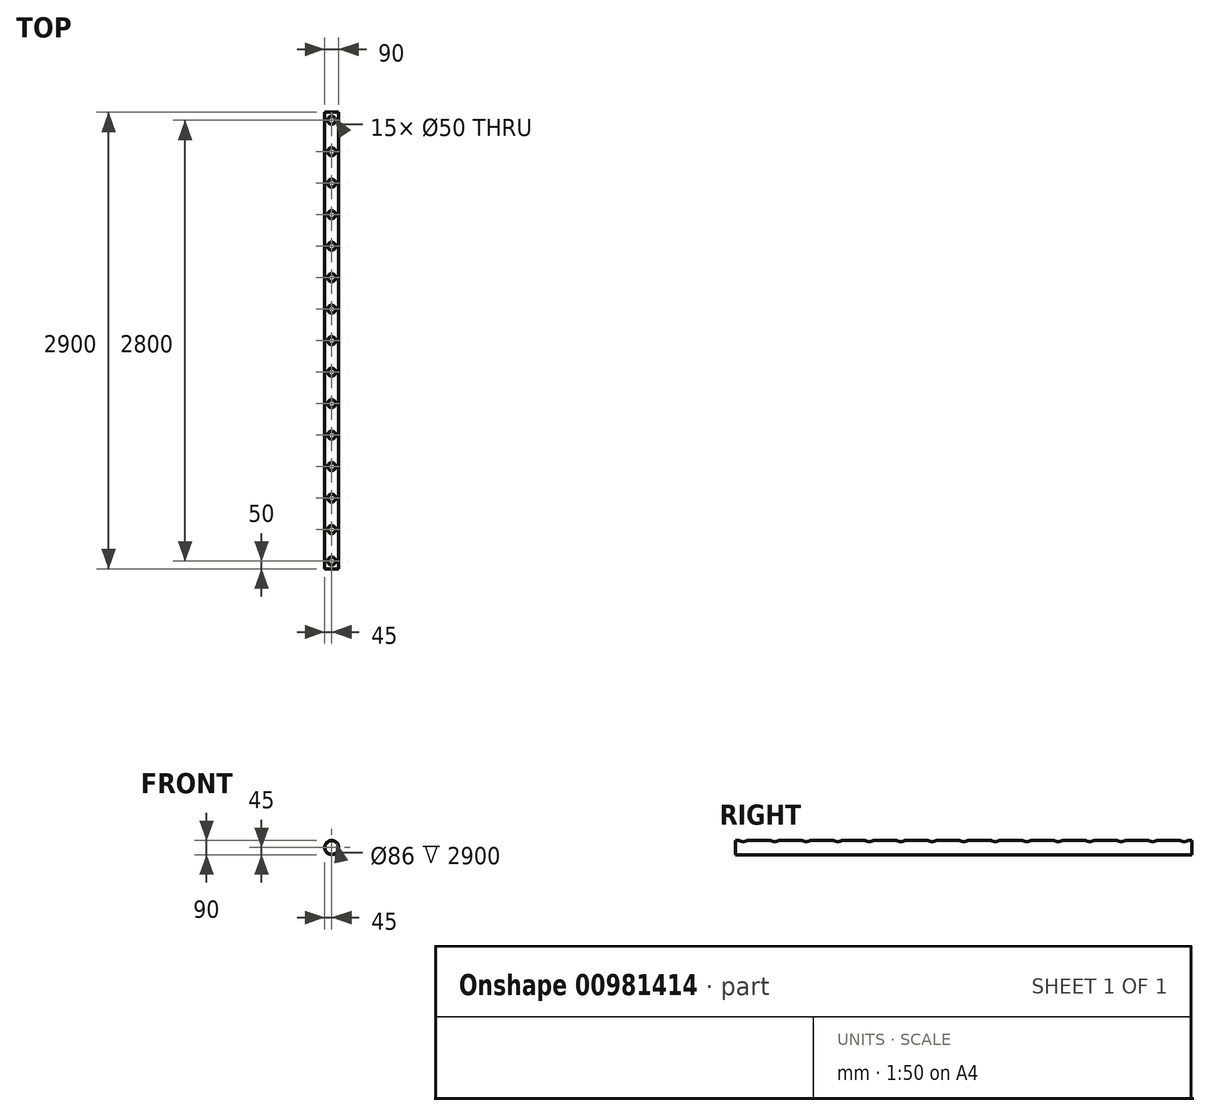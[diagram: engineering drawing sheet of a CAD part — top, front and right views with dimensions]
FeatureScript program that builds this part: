
annotation { "Feature Type Name" : "Feature", "Feature Type Description" : "" }
export const myFeature = defineFeature(function(context is Context, id is Id, definition is map)
    precondition{}
    {
        {
            var Q0;
            Q0=qCreatedBy(makeId("Front.planeOp"),FACE);
            var sketch = newSketch(context, id + "F0", { "sketchPlane" : qUnion([Q0])});
            skCircle(sketch, "E0", {"center": v(0, 0) * mm, "radius": 45 * mm});
            skCircle(sketch, "E1.0", {"center": v(0, 0) * mm, "radius": 43 * mm});
            skSolve(sketch);
        }
        {
            var Q0;
            Q0=qSketchRegion(id+"F0",true);
            extrude(context, id + "F1", {"entities" : qUnion([Q0]), "endBound" : BoundingType.SYMMETRIC, "depth" : 2900 * mm, "offsetDistance" : 25 * mm});
        }
        {
            var Q0;
            Q0=qCreatedBy(makeId("Top.planeOp"),FACE);
            cPlane(context, id + "F2", {"entities" : qUnion([Q0]), "cplaneType" : CPlaneType.OFFSET, "offset" : 45 * mm, "width" : 150 * mm, "height" : 150 * mm});
        }
        {
            var Q0;
            Q0=qCreatedBy(id+"F2.planeOp",FACE);
            var sketch = newSketch(context, id + "F3", { "sketchPlane" : qUnion([Q0])});
            skPoint(sketch, "E2", {"position": v(0, -1400) * mm});
            skPoint(sketch, "E3", {"position": v(0, -1200) * mm});
            skPoint(sketch, "E4", {"position": v(0, -1000) * mm});
            skPoint(sketch, "E5", {"position": v(0, -800) * mm});
            skPoint(sketch, "E6", {"position": v(0, -600) * mm});
            skPoint(sketch, "E7", {"position": v(0, -400) * mm});
            skPoint(sketch, "E8", {"position": v(0, -200) * mm});
            skPoint(sketch, "E9", {"position": v(0, 0) * mm});
            skPoint(sketch, "E10", {"position": v(0, 200) * mm});
            skPoint(sketch, "E11", {"position": v(0, 400) * mm});
            skPoint(sketch, "E12", {"position": v(0, 600) * mm});
            skPoint(sketch, "E13", {"position": v(0, 800) * mm});
            skPoint(sketch, "E14", {"position": v(0, 1000) * mm});
            skPoint(sketch, "E15", {"position": v(0, 1200) * mm});
            skPoint(sketch, "E16", {"position": v(0, 1400) * mm});
            skSolve(sketch);
        }
        {
            var Q0;
            Q0=sQuery(id+"F3.wireOp",VERTEX,"E2");
            var Q1;
            Q1=sQuery(id+"F3.wireOp",VERTEX,"E3");
            var Q2;
            Q2=sQuery(id+"F3.wireOp",VERTEX,"E4");
            var Q3;
            Q3=sQuery(id+"F3.wireOp",VERTEX,"E5");
            var Q4;
            Q4=sQuery(id+"F3.wireOp",VERTEX,"E6");
            var Q5;
            Q5=sQuery(id+"F3.wireOp",VERTEX,"E7");
            var Q6;
            Q6=sQuery(id+"F3.wireOp",VERTEX,"E8");
            var Q7;
            Q7=sQuery(id+"F3.wireOp",VERTEX,"E9");
            var Q8;
            Q8=sQuery(id+"F3.wireOp",VERTEX,"E10");
            var Q9;
            Q9=sQuery(id+"F3.wireOp",VERTEX,"E11");
            var Q10;
            Q10=sQuery(id+"F3.wireOp",VERTEX,"E12");
            var Q11;
            Q11=sQuery(id+"F3.wireOp",VERTEX,"E13");
            var Q12;
            Q12=sQuery(id+"F3.wireOp",VERTEX,"E14");
            var Q13;
            Q13=sQuery(id+"F3.wireOp",VERTEX,"E15");
            var Q14;
            Q14=sQuery(id+"F3.wireOp",VERTEX,"E16");
            var Q15;
            Q15=sQuery(id+"F3.wireOp",VERTEX,"f4cd902c-7ee6-44a1-aa6d-15636b985a91");
            var Q16;
            Q16=sQuery(id+"F3.wireOp",VERTEX,"a0becd45-3f8c-473a-b9c5-eca89ffffb86");
            var Q17;
            Q17=sQuery(id+"F3.wireOp",VERTEX,"449d03d7-6090-459a-adaf-9611daa20e82");
            var Q18;
            Q18=sQuery(id+"F3.wireOp",VERTEX,"1d2369e2-f7b6-45cb-9ac7-ef4d2139859a");
            var Q19;
            Q19=sQuery(id+"F3.wireOp",VERTEX,"4217ffee-23aa-4e57-b56b-1031955cdd20");
            var Q20;
            Q20=sQuery(id+"F3.wireOp",VERTEX,"f9e667d2-43f0-46cb-85dd-7700daad2ab1");
            var Q21;
            Q21=sQuery(id+"F3.wireOp",VERTEX,"a141cc4f-d6fa-4136-a428-d91cc8b08e23");
            var Q22;
            Q22=sQuery(id+"F3.wireOp",VERTEX,"6950c5e6-caf7-4953-8c5b-56709a9cffe9");
            var Q23;
            Q23=sQuery(id+"F3.wireOp",VERTEX,"1581daf2-9304-4365-a3cc-e960652a3bf4");
            var Q24;
            Q24=sQuery(id+"F3.wireOp",VERTEX,"25a0b738-50ad-46bb-ba52-db4eb22869ea");
            var Q25;
            Q25=sQuery(id+"F3.wireOp",VERTEX,"23c6b068-1da5-4682-a93c-07f6e733a235");
            var Q26;
            Q26=sQuery(id+"F3.wireOp",VERTEX,"77491461-51bd-4097-a69a-b50156a0fef7");
            var Q27;
            Q27=sQuery(id+"F3.wireOp",VERTEX,"89e2eaf9-af87-4198-a739-5b01357332c3");
            var Q28;
            Q28=sQuery(id+"F3.wireOp",VERTEX,"a31ac070-19d1-4092-b391-6f630edb761b");
            var Q29;
            Q29=makeQuery(id+"F1.opExtrude","SWEPT_BODY",BODY,{"disambiguationData":[OSD([sQuery(id+"F0.wireOp",EDGE,"E0"),sQuery(id+"F0.wireOp",EDGE,"E1.0")])]});
            hole(context, id + "F4", {"style" : HoleStyle.SIMPLE, "endStyle" : HoleEndStyle.BLIND, "holeDiameter" : 50 * mm, "majorDiameter" : 5 * mm, "holeDepth" : 50 * mm, "isTappedThrough" : true, "tappedDepth" : 12 * mm, "tapClearance" : 3, "startFromSketch" : true, "locations" : qUnion([Q0, Q1, Q2, Q3, Q4, Q5, Q6, Q7, Q8, Q9, Q10, Q11, Q12, Q13, Q14, Q15, Q16, Q17, Q18, Q19, Q20, Q21, Q22, Q23, Q24, Q25, Q26, Q27, Q28]), "scope" : qUnion([Q29])});
        }
    });
